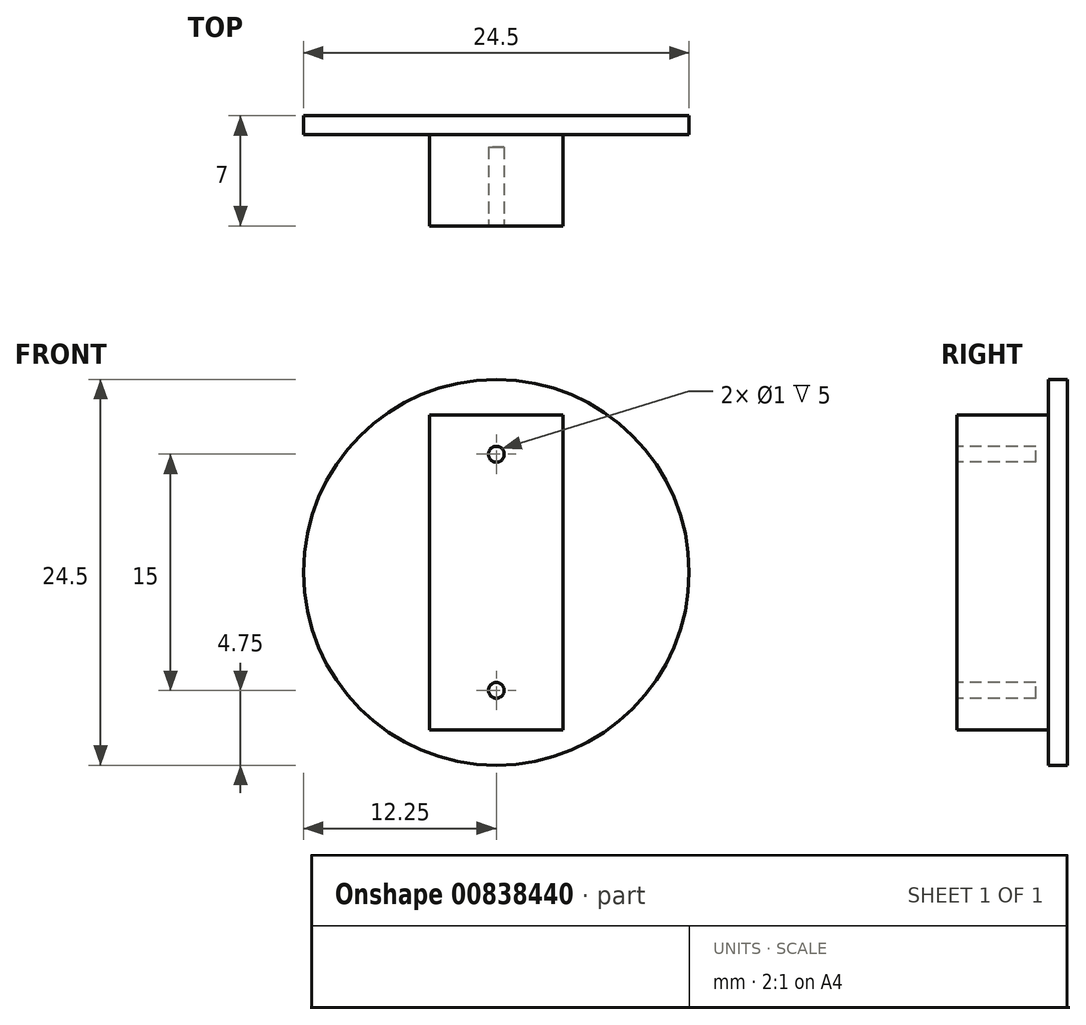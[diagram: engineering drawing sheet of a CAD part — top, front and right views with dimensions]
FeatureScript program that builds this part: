
annotation { "Feature Type Name" : "Feature", "Feature Type Description" : "" }
export const myFeature = defineFeature(function(context is Context, id is Id, definition is map)
    precondition{}
    {
        {
            var Q0;
            Q0=qCreatedBy(makeId("Front.planeOp"),FACE);
            var sketch = newSketch(context, id + "F0", { "sketchPlane" : qUnion([Q0])});
            skCircle(sketch, "E0", {"center": v(0, 0) * mm, "radius": 12.25 * mm});
            skLineSegment(sketch, "E1.bottom", {"start": v(4.25, 10) * mm, "end": v(-4.25, 10) * mm});
            skLineSegment(sketch, "E1.top", {"start": v(4.25, -10) * mm, "end": v(-4.25, -10) * mm});
            skLineSegment(sketch, "E1.left", {"start": v(4.25, 10) * mm, "end": v(4.25, -10) * mm});
            skLineSegment(sketch, "E1.right", {"start": v(-4.25, 10) * mm, "end": v(-4.25, -10) * mm});
            skSolve(sketch);
        }
        {
            var Q0;
            Q0=makeQuery(id+"F0.imprint","IMPRINT",FACE,{"disambiguationData":[TD([[makeQuery(id+"F0.imprint","IMPRINT",EDGE,{"derivedFrom":sQuery(id+"F0.wireOp",EDGE,"E0")}),1.0]])]});
            extrude(context, id + "F1", {"entities" : qUnion([Q0]), "depth" : 1.2 * mm, "offsetDistance" : 25 * mm});
        }
        {
            var Q0;
            Q0=makeQuery(id+"F0.imprint","IMPRINT",FACE,{"disambiguationData":[TD([[makeQuery(id+"F0.imprint","IMPRINT",EDGE,{"derivedFrom":sQuery(id+"F0.wireOp",EDGE,"E1.bottom")}),1.0]])]});
            extrude(context, id + "F2", {"entities" : qUnion([Q0]), "operationType" : NewBodyOperationType.ADD, "depth" : 7 * mm, "offsetDistance" : 25 * mm});
        }
        {
            var Q0;
            Q0=makeQuery(id+"F2.opExtrude","CAP_FACE",FACE,{"disambiguationData":[OSD([sQuery(id+"F0.wireOp",EDGE,"E1.bottom"),sQuery(id+"F0.wireOp",EDGE,"E1.top"),sQuery(id+"F0.wireOp",EDGE,"E1.left"),sQuery(id+"F0.wireOp",EDGE,"E1.right")])],"isStart":false});
            var sketch = newSketch(context, id + "F3", { "sketchPlane" : qUnion([Q0])});
            skCircle(sketch, "E2", {"center": v(0, 7.5) * mm, "radius": 0.5 * mm});
            skCircle(sketch, "E3", {"center": v(0, -7.5) * mm, "radius": 0.5 * mm});
            skSolve(sketch);
        }
        {
            var Q0;
            Q0=makeQuery(id+"F3.imprint","IMPRINT",FACE,{"disambiguationData":[TD([[makeQuery(id+"F3.imprint","IMPRINT",EDGE,{"derivedFrom":sQuery(id+"F3.wireOp",EDGE,"E3")}),1.0]])]});
            var Q1;
            Q1=makeQuery(id+"F3.imprint","IMPRINT",FACE,{"disambiguationData":[TD([[makeQuery(id+"F3.imprint","IMPRINT",EDGE,{"derivedFrom":sQuery(id+"F3.wireOp",EDGE,"E2")}),1.0]])]});
            extrude(context, id + "F4", {"entities" : qUnion([Q0, Q1]), "operationType" : NewBodyOperationType.REMOVE, "oppositeDirection" : true, "depth" : 5 * mm, "offsetDistance" : 25 * mm});
        }
    });
